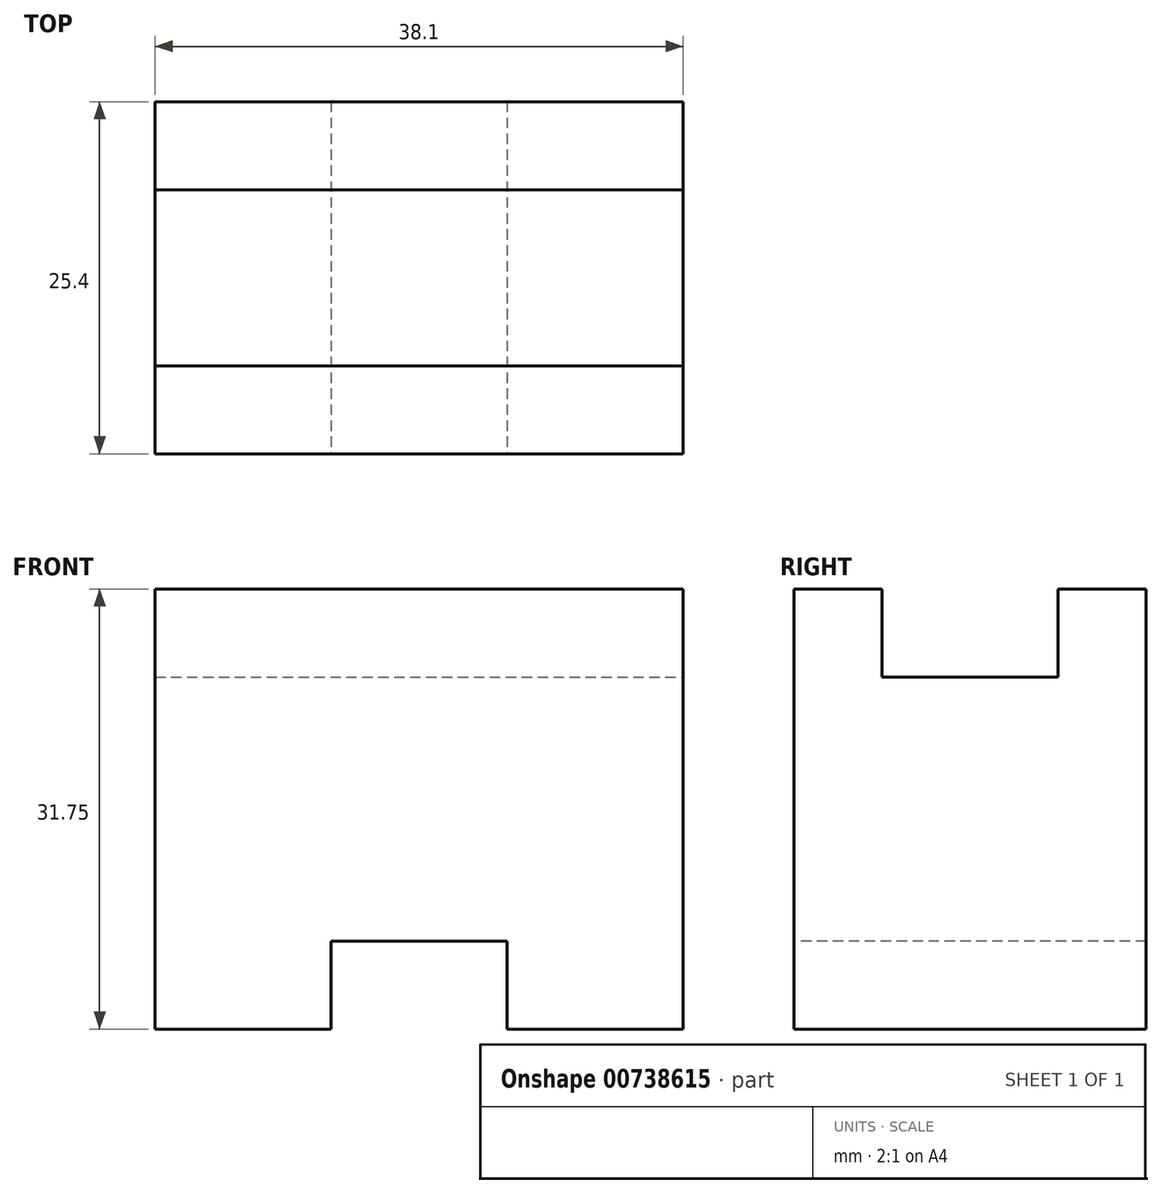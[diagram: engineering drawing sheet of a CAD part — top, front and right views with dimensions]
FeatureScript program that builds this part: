
annotation { "Feature Type Name" : "Feature", "Feature Type Description" : "" }
export const myFeature = defineFeature(function(context is Context, id is Id, definition is map)
    precondition{}
    {
        {
            var Q0;
            Q0=qCreatedBy(makeId("Front.planeOp"),FACE);
            var sketch = newSketch(context, id + "F0", { "sketchPlane" : qUnion([Q0])});
            skLineSegment(sketch, "E0.bottom", {"start": v(0, 0) * mm, "end": v(38.1, 0) * mm});
            skLineSegment(sketch, "E0.top", {"start": v(0, 31.75) * mm, "end": v(38.1, 31.75) * mm});
            skLineSegment(sketch, "E0.left", {"start": v(0, 0) * mm, "end": v(0, 31.75) * mm});
            skLineSegment(sketch, "E0.right", {"start": v(38.1, 0) * mm, "end": v(38.1, 31.75) * mm});
            skSolve(sketch);
        }
        {
            var Q0;
            Q0=makeQuery(id+"F0.imprint","IMPRINT",FACE,{"disambiguationData":[TD([[makeQuery(id+"F0.imprint","IMPRINT",EDGE,{"derivedFrom":sQuery(id+"F0.wireOp",EDGE,"E0.bottom")}),1.0]])]});
            extrude(context, id + "F1", {"entities" : qUnion([Q0]), "depth" : 25.4 * mm, "offsetDistance" : 25.4 * mm});
        }
        {
            var Q0;
            Q0=makeQuery(id+"F1.opExtrude","SWEPT_FACE",FACE,{"disambiguationData":[OSD([sQuery(id+"F0.wireOp",EDGE,"E0.top")])]});
            var sketch = newSketch(context, id + "F2", { "sketchPlane" : qUnion([Q0])});
            skLineSegment(sketch, "E1", {"start": v(0, 0) * mm, "end": v(0, -6.35) * mm});
            skLineSegment(sketch, "E2.bottom", {"start": v(0, -6.35) * mm, "end": v(38.1, -6.35) * mm});
            skLineSegment(sketch, "E2.top", {"start": v(0, -19.05) * mm, "end": v(38.1, -19.05) * mm});
            skLineSegment(sketch, "E2.left", {"start": v(0, -6.35) * mm, "end": v(0, -19.05) * mm});
            skLineSegment(sketch, "E2.right", {"start": v(38.1, -6.35) * mm, "end": v(38.1, -19.05) * mm});
            skSolve(sketch);
        }
        {
            var Q0;
            Q0=makeQuery(id+"F2.imprint","IMPRINT",FACE,{"disambiguationData":[TD([[makeQuery(id+"F2.imprint","IMPRINT",EDGE,{"derivedFrom":sQuery(id+"F2.wireOp",EDGE,"E2.bottom")}),-1.0]])]});
            extrude(context, id + "F3", {"entities" : qUnion([Q0]), "operationType" : NewBodyOperationType.REMOVE, "oppositeDirection" : true, "depth" : 6.35 * mm, "offsetDistance" : 25.4 * mm});
        }
        {
            var Q0;
            Q0=makeQuery(id+"F1.opExtrude","CAP_FACE",FACE,{"disambiguationData":[OSD([sQuery(id+"F0.wireOp",EDGE,"E0.bottom"),sQuery(id+"F0.wireOp",EDGE,"E0.top"),sQuery(id+"F0.wireOp",EDGE,"E0.left"),sQuery(id+"F0.wireOp",EDGE,"E0.right")])],"isStart":false});
            var sketch = newSketch(context, id + "F4", { "sketchPlane" : qUnion([Q0])});
            skLineSegment(sketch, "E3", {"start": v(0, 0) * mm, "end": v(12.7, 0) * mm});
            skLineSegment(sketch, "E4.bottom", {"start": v(12.7, 0) * mm, "end": v(25.4, 0) * mm});
            skLineSegment(sketch, "E4.top", {"start": v(12.7, 6.35) * mm, "end": v(25.4, 6.35) * mm});
            skLineSegment(sketch, "E4.left", {"start": v(12.7, 0) * mm, "end": v(12.7, 6.35) * mm});
            skLineSegment(sketch, "E4.right", {"start": v(25.4, 0) * mm, "end": v(25.4, 6.35) * mm});
            skSolve(sketch);
        }
        {
            var Q0;
            Q0=makeQuery(id+"F4.imprint","IMPRINT",FACE,{"disambiguationData":[TD([[makeQuery(id+"F4.imprint","IMPRINT",EDGE,{"derivedFrom":sQuery(id+"F4.wireOp",EDGE,"E4.bottom")}),1.0]])]});
            extrude(context, id + "F5", {"entities" : qUnion([Q0]), "operationType" : NewBodyOperationType.REMOVE, "oppositeDirection" : true, "depth" : 25.4 * mm, "offsetDistance" : 25.4 * mm});
        }
    });
